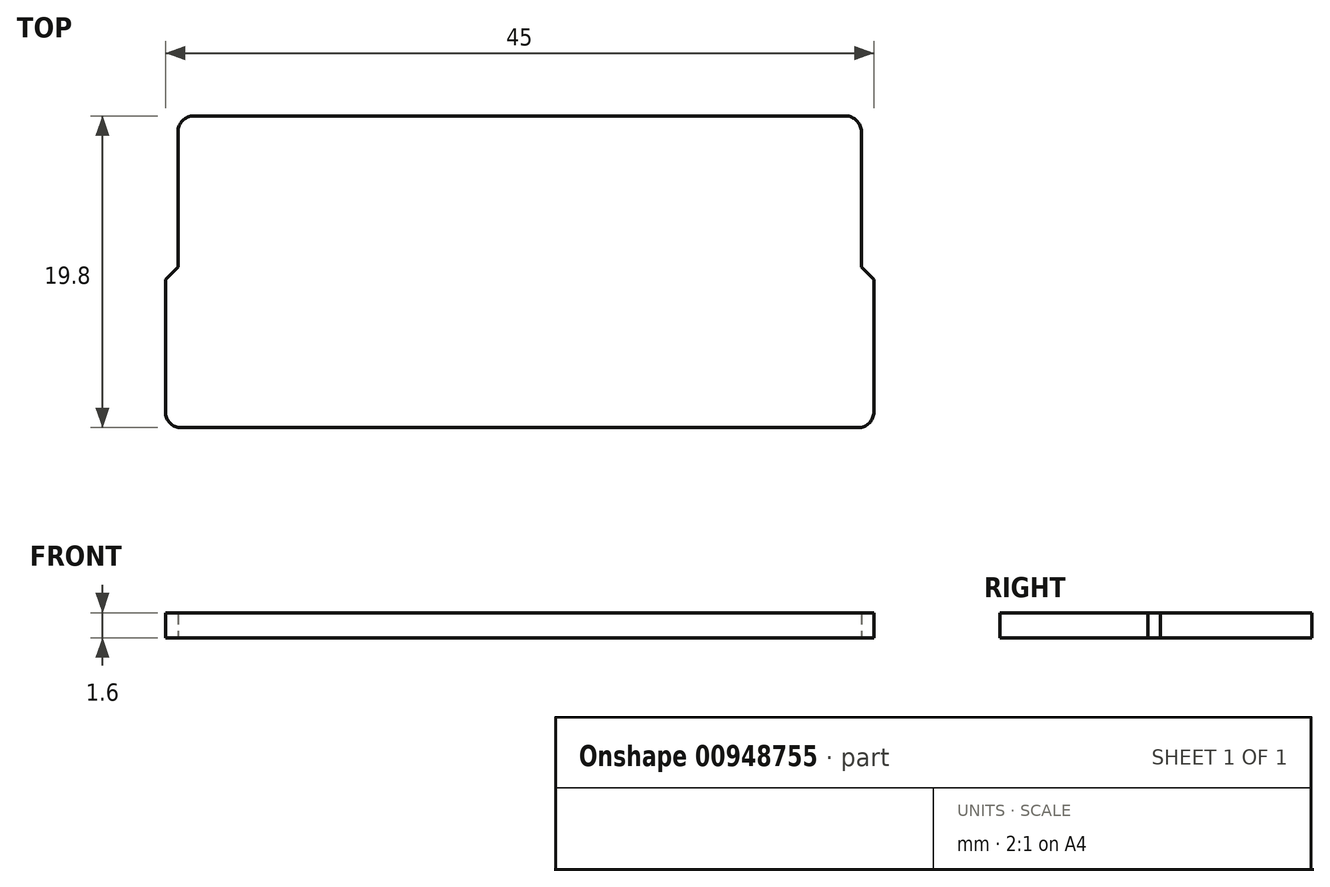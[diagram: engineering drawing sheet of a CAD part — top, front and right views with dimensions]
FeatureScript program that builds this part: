
annotation { "Feature Type Name" : "Feature", "Feature Type Description" : "" }
export const myFeature = defineFeature(function(context is Context, id is Id, definition is map)
    precondition{}
    {
        {
            var Q0;
            Q0=qCreatedBy(makeId("Top.planeOp"),FACE);
            var sketch = newSketch(context, id + "F0", { "sketchPlane" : qUnion([Q0])});
            skLineSegment(sketch, "E0", {"start": v(-18.71, -7.8) * mm, "end": v(26.29, -7.8) * mm});
            skLineSegment(sketch, "E1", {"start": v(26.29, -7.8) * mm, "end": v(26.29, 1.6) * mm});
            skLineSegment(sketch, "E2", {"start": v(25.49, 2.4) * mm, "end": v(25.49, 12) * mm});
            skLineSegment(sketch, "E3", {"start": v(25.49, 12) * mm, "end": v(-17.91, 12) * mm});
            skLineSegment(sketch, "E4", {"start": v(-17.91, 12) * mm, "end": v(-17.91, 2.4) * mm});
            skLineSegment(sketch, "E5", {"start": v(-18.71, 1.6) * mm, "end": v(-18.71, -7.8) * mm});
            skLineSegment(sketch, "E6", {"start": v(26.29, 1.6) * mm, "end": v(25.49, 2.4) * mm});
            skLineSegment(sketch, "E7", {"start": v(-18.71, 1.6) * mm, "end": v(-17.91, 2.4) * mm});
            skSolve(sketch);
        }
        {
            var Q0;
            Q0=makeQuery(id+"F0.imprint","IMPRINT",FACE,{"disambiguationData":[TD([[makeQuery(id+"F0.imprint","IMPRINT",EDGE,{"derivedFrom":sQuery(id+"F0.wireOp",EDGE,"E0")}),1.0]])]});
            extrude(context, id + "F1", {"entities" : qUnion([Q0]), "depth" : 1.6 * mm, "offsetDistance" : 25 * mm});
        }
        {
            var Q0;
            Q0=makeQuery(id+"F1.opExtrude","SWEPT_EDGE",EDGE,{"disambiguationData":[OSD([sQuery(id+"F0.wireOp",EDGE,"E0"),sQuery(id+"F0.wireOp",EDGE,"E5")])]});
            var Q1;
            Q1=makeQuery(id+"F1.opExtrude","SWEPT_EDGE",EDGE,{"disambiguationData":[OSD([sQuery(id+"F0.wireOp",EDGE,"E0"),sQuery(id+"F0.wireOp",EDGE,"E1")])]});
            var Q2;
            Q2=makeQuery(id+"F1.opExtrude","SWEPT_EDGE",EDGE,{"disambiguationData":[OSD([sQuery(id+"F0.wireOp",EDGE,"E3"),sQuery(id+"F0.wireOp",EDGE,"E4")])]});
            var Q3;
            Q3=makeQuery(id+"F1.opExtrude","SWEPT_EDGE",EDGE,{"disambiguationData":[OSD([sQuery(id+"F0.wireOp",EDGE,"E2"),sQuery(id+"F0.wireOp",EDGE,"E3")])]});
            fillet(context, id + "F2", {"entities" : qUnion([Q0, Q1, Q2, Q3]), "radius" : 1 * mm, "tangentPropagation" : true, "allowEdgeOverflow" : false});
        }
    });
